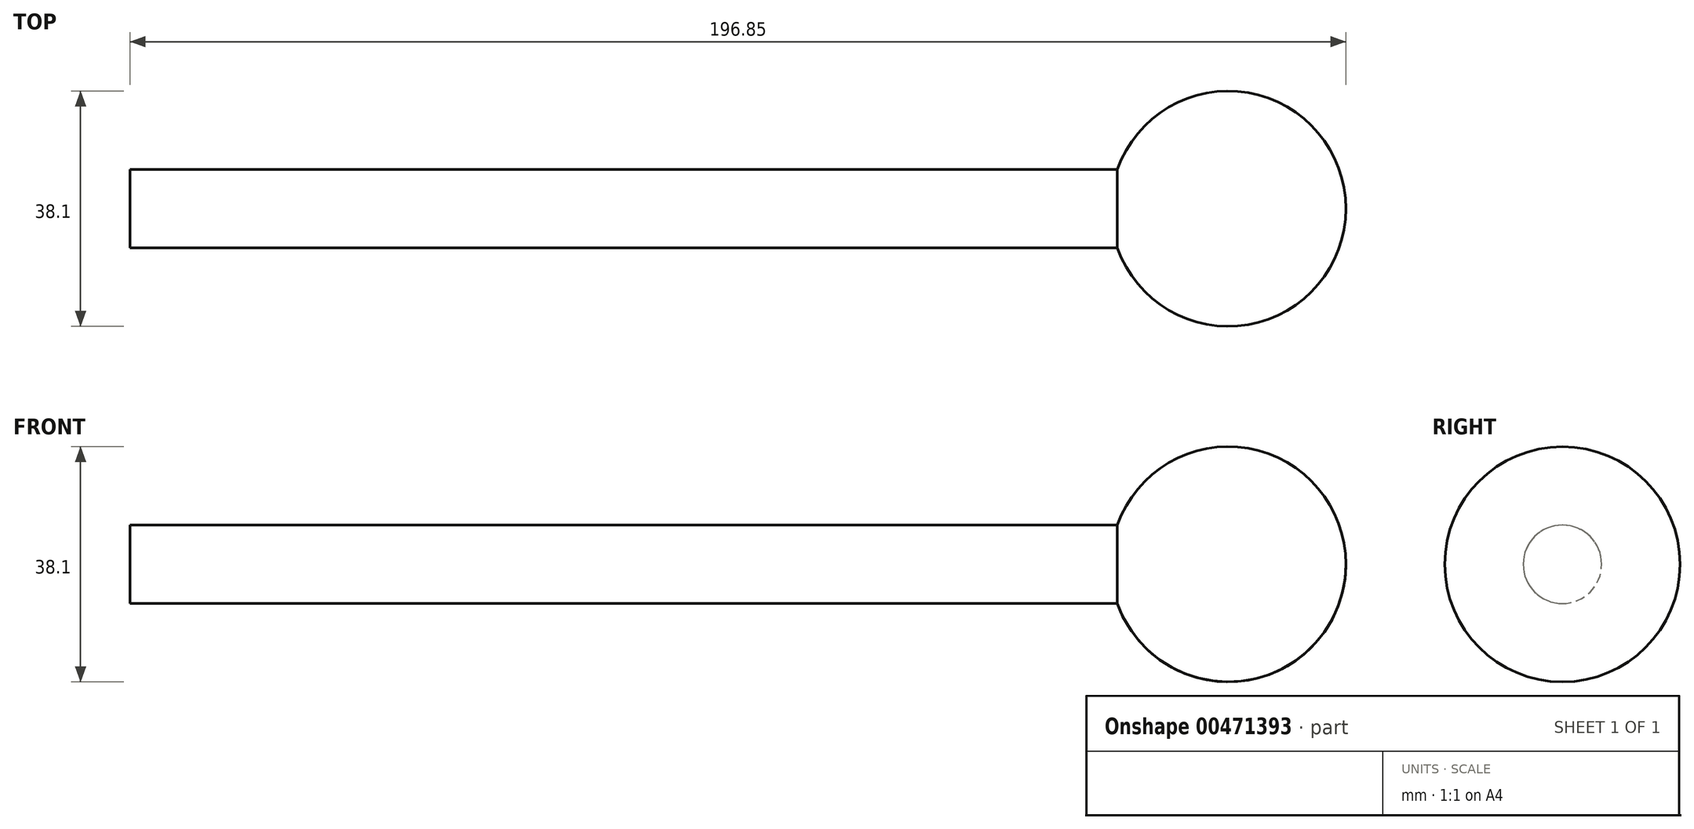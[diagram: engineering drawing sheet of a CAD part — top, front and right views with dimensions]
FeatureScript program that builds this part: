
annotation { "Feature Type Name" : "Feature", "Feature Type Description" : "" }
export const myFeature = defineFeature(function(context is Context, id is Id, definition is map)
    precondition{}
    {
        {
            var Q0;
            Q0=qCreatedBy(makeId("Front.planeOp"),FACE);
            var sketch = newSketch(context, id + "F0", { "sketchPlane" : qUnion([Q0])});
            skLineSegment(sketch, "E0.bottom", {"start": v(0, 0) * mm, "end": v(177.8, 0) * mm});
            skLineSegment(sketch, "E0.top", {"start": v(0, 6.35) * mm, "end": v(177.8, 6.35) * mm});
            skLineSegment(sketch, "E0.left", {"start": v(0, 0) * mm, "end": v(0, 6.35) * mm});
            skLineSegment(sketch, "E0.right", {"start": v(177.8, 0) * mm, "end": v(177.8, 6.35) * mm});
            skArc(sketch, "E1", {"start": v(158.75, 6.35) * mm, "mid": v(177.8, -12.7) * mm, "end": v(196.85, 6.35) * mm});
            skLineSegment(sketch, "E2", {"start": v(158.75, 6.35) * mm, "end": v(196.85, 6.35) * mm});
            skSolve(sketch);
        }
        {
            var Q0;
            Q0 = qSketchRegion(id + "F0", true);
            var Q1;
            Q1=sQuery(id+"F0.wireOp",EDGE,"E0.top");
            revolve(context, id + "F1", {"entities" : qUnion([Q0]), "axis" : qUnion([Q1]), "revolveType" : RevolveType.FULL});
        }
    });
